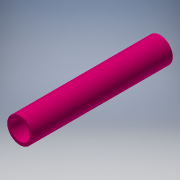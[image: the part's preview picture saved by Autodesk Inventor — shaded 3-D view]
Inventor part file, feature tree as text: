
AUTODESK INVENTOR PART (.ipt)
format: ipt  version: 2018.2 (Build 222227000, 227)  size: 109,568 bytes
history: native  units: in
note: dims shown in document units (in); Inventor stores cm internally (conversion verified against a paired STEP export)
features: extrude x1, sketch x1
ambient origin geometry x8: Origin, YZ Plane, XZ Plane, XY Plane, X Axis, Y Axis, Z Axis, Center Point
bodies: Solid1 (feature_tree)
feature tree (2):
  extrude  "Extrusion1"  Depth=7.25in
  sketch  "Sketch1"  dims[d0=1.315in d1=1.0in d2=7.25in d3=0.0in]
